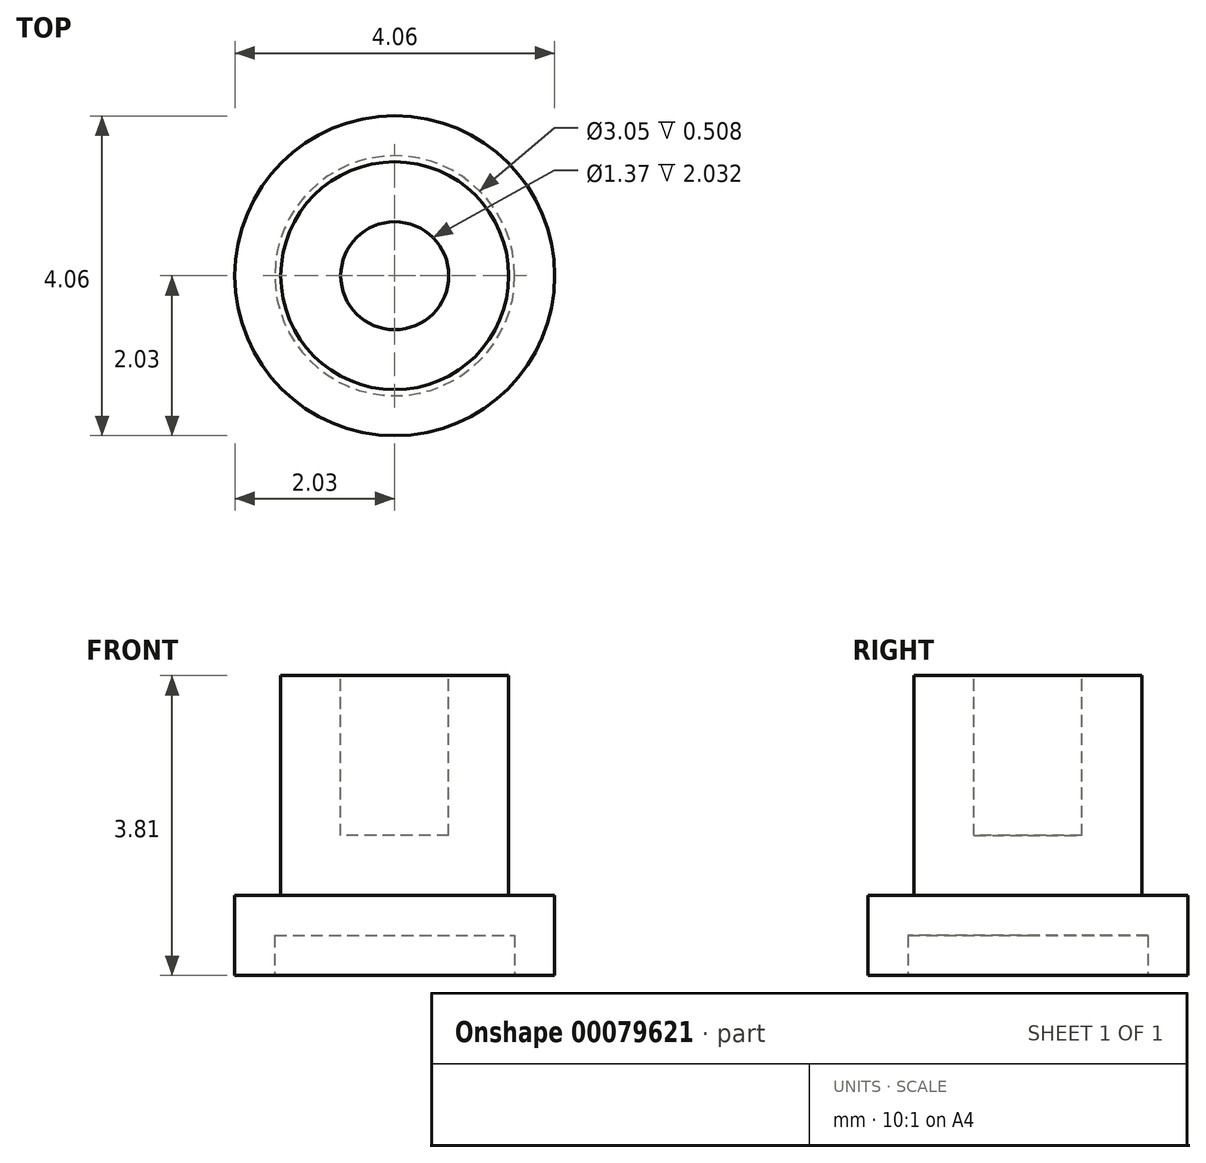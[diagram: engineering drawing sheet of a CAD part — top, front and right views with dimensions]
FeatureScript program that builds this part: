
annotation { "Feature Type Name" : "Feature", "Feature Type Description" : "" }
export const myFeature = defineFeature(function(context is Context, id is Id, definition is map)
    precondition{}
    {
        {
            var Q0;
            Q0=qCreatedBy(makeId("Top.planeOp"),FACE);
            var sketch = newSketch(context, id + "F0", { "sketchPlane" : qUnion([Q0])});
            skCircle(sketch, "E0", {"center": v(0, 0) * mm, "radius": 1.45 * mm});
            skSolve(sketch);
        }
        {
            var Q0;
            Q0 = qSketchRegion(id + "F0", true);
            extrude(context, id + "F1", {"entities" : qUnion([Q0]), "depth" : 3.8 * mm});
        }
        {
            var Q0;
            Q0=qCreatedBy(makeId("Top.planeOp"),FACE);
            var sketch = newSketch(context, id + "F2", { "sketchPlane" : qUnion([Q0])});
            skCircle(sketch, "E1", {"center": v(0, 0) * mm, "radius": 2.03 * mm});
            skSolve(sketch);
        }
        {
            var Q0;
            Q0 = qSketchRegion(id + "F2", true);
            extrude(context, id + "F3", {"entities" : qUnion([Q0]), "operationType" : NewBodyOperationType.ADD, "depth" : 1.02 * mm});
        }
        {
            var Q0;
            Q0=makeQuery(id+"F3.boolean.opBoolean","MERGE",FACE,{"derivedFrom":[makeQuery(id+"F1.opExtrude","CAP_FACE",FACE,{"disambiguationData":[OSD([sQuery(id+"F0.wireOp",EDGE,"E0")])],"isStart":true}),makeQuery(id+"F3.opExtrude","CAP_FACE",FACE,{"disambiguationData":[OSD([sQuery(id+"F2.wireOp",EDGE,"E1")])],"isStart":true})]});
            var sketch = newSketch(context, id + "F4", { "sketchPlane" : qUnion([Q0])});
            skCircle(sketch, "E2", {"center": v(0, 0) * mm, "radius": 1.52 * mm});
            skSolve(sketch);
        }
        {
            var Q0;
            Q0 = qSketchRegion(id + "F4", true);
            extrude(context, id + "F5", {"entities" : qUnion([Q0]), "operationType" : NewBodyOperationType.REMOVE, "oppositeDirection" : true, "depth" : 0.5 * mm});
        }
        {
            var Q0;
            Q0=makeQuery(id+"F1.opExtrude","CAP_FACE",FACE,{"disambiguationData":[OSD([sQuery(id+"F0.wireOp",EDGE,"E0")])],"isStart":false});
            var sketch = newSketch(context, id + "F6", { "sketchPlane" : qUnion([Q0])});
            skCircle(sketch, "E3", {"center": v(0, 0) * mm, "radius": 0.69 * mm});
            skSolve(sketch);
        }
        {
            var Q0;
            Q0 = qSketchRegion(id + "F6", true);
            extrude(context, id + "F7", {"entities" : qUnion([Q0]), "operationType" : NewBodyOperationType.REMOVE, "oppositeDirection" : true, "depth" : 2.03 * mm});
        }
    });
